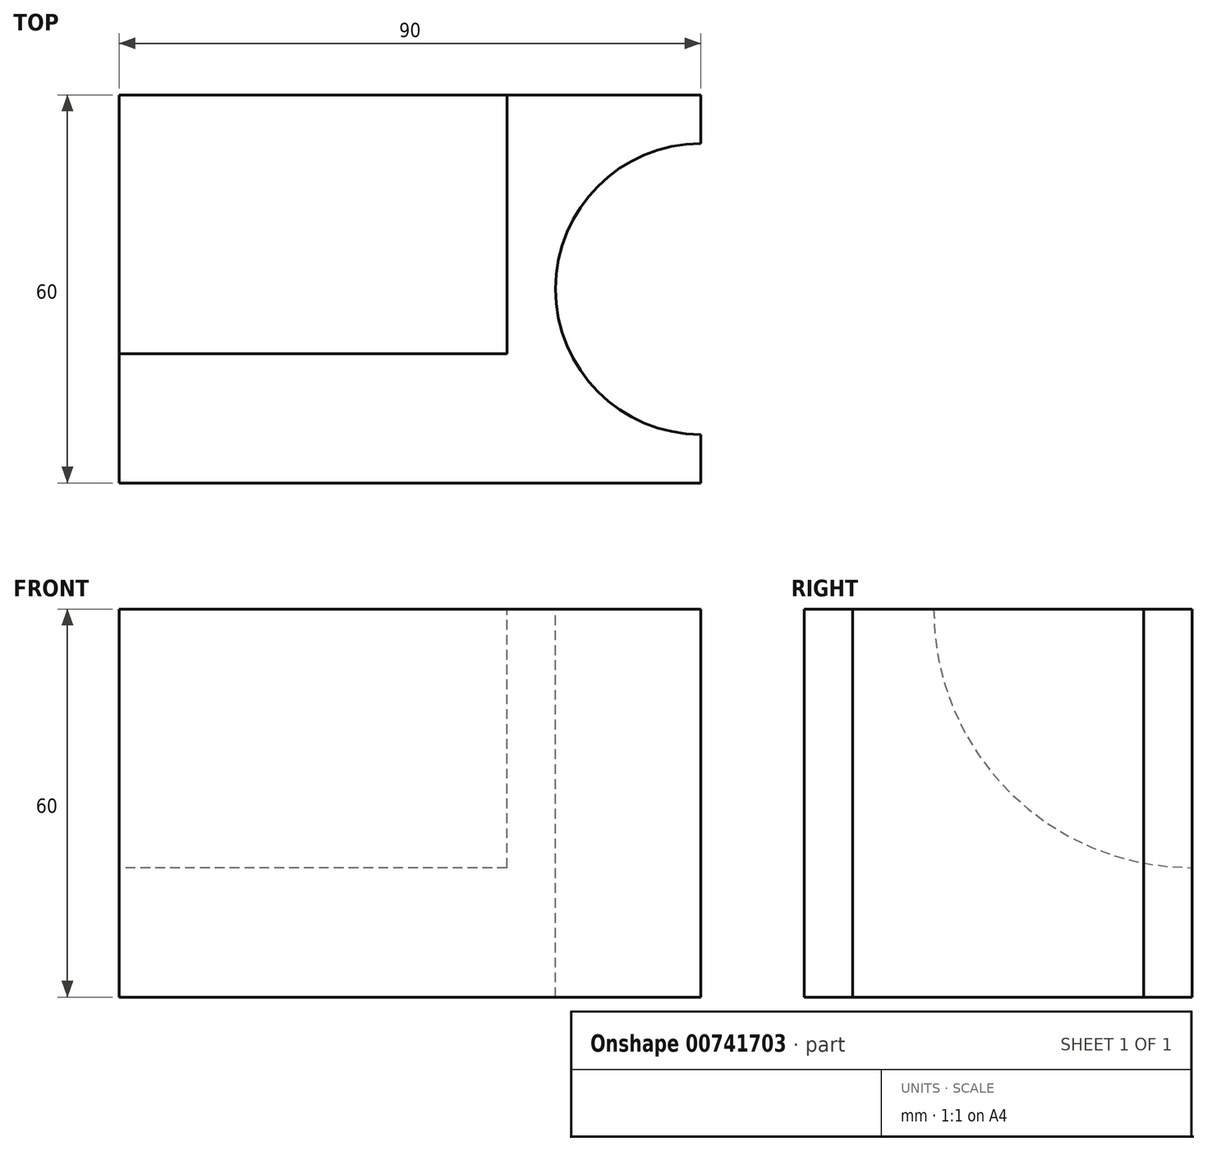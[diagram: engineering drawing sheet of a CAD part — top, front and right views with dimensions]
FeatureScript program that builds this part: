
annotation { "Feature Type Name" : "Feature", "Feature Type Description" : "" }
export const myFeature = defineFeature(function(context is Context, id is Id, definition is map)
    precondition{}
    {
        {
            var Q0;
            Q0=qCreatedBy(makeId("Front.planeOp"),FACE);
            var sketch = newSketch(context, id + "F0", { "sketchPlane" : qUnion([Q0])});
            skLineSegment(sketch, "E0.bottom", {"start": v(-45, -30) * mm, "end": v(45, -30) * mm});
            skLineSegment(sketch, "E0.top", {"start": v(-45, 30) * mm, "end": v(45, 30) * mm});
            skLineSegment(sketch, "E0.left", {"start": v(-45, -30) * mm, "end": v(-45, 30) * mm});
            skLineSegment(sketch, "E0.right", {"start": v(45, -30) * mm, "end": v(45, 30) * mm});
            skPoint(sketch, "E0.middle", {"position": v(0, 0) * mm});
            skSolve(sketch);
        }
        {
            var Q0;
            Q0=makeQuery(id+"F0.imprint","IMPRINT",FACE,{"disambiguationData":[TD([[makeQuery(id+"F0.imprint","IMPRINT",EDGE,{"derivedFrom":sQuery(id+"F0.wireOp",EDGE,"E0.bottom")}),1.0]])]});
            extrude(context, id + "F1", {"entities" : qUnion([Q0]), "depth" : 60 * mm, "offsetDistance" : 25 * mm});
        }
        {
            var Q0;
            Q0=makeQuery(id+"F1.opExtrude","SWEPT_FACE",FACE,{"disambiguationData":[OSD([sQuery(id+"F0.wireOp",EDGE,"E0.top")])]});
            var sketch = newSketch(context, id + "F2", { "sketchPlane" : qUnion([Q0])});
            skArc(sketch, "E1", {"start": v(45, -7.5) * mm, "mid": v(22.5, -30) * mm, "end": v(45, -52.5) * mm});
            skSolve(sketch);
        }
        {
            var Q0;
            {var subQ0=sQuery(id+"F2.wireOp",EDGE,"E1");Q0=makeQuery(id+"F2.imprint","IMPRINT",FACE,{"disambiguationData":[TD([[makeQuery(id+"F2.imprint","IMPRINT",EDGE,{"derivedFrom":subQ0}),1.0]])]});}
            extrude(context, id + "F3", {"entities" : qUnion([Q0]), "operationType" : NewBodyOperationType.REMOVE, "endBound" : BoundingType.THROUGH_ALL, "oppositeDirection" : true, "depth" : 25 * mm, "offsetDistance" : 25 * mm});
        }
        {
            var Q0;
            Q0=makeQuery(id+"F1.opExtrude","SWEPT_FACE",FACE,{"disambiguationData":[OSD([sQuery(id+"F0.wireOp",EDGE,"E0.left")])]});
            var sketch = newSketch(context, id + "F4", { "sketchPlane" : qUnion([Q0])});
            skArc(sketch, "E2", {"start": v(0, -10) * mm, "mid": v(28.28, 1.72) * mm, "end": v(40, 30) * mm});
            skSolve(sketch);
        }
        {
            var Q0;
            {var subQ0=sQuery(id+"F4.wireOp",EDGE,"E2");Q0=makeQuery(id+"F4.imprint","IMPRINT",FACE,{"disambiguationData":[TD([[makeQuery(id+"F4.imprint","IMPRINT",EDGE,{"derivedFrom":subQ0}),1.0]])]});}
            extrude(context, id + "F5", {"entities" : qUnion([Q0]), "operationType" : NewBodyOperationType.REMOVE, "oppositeDirection" : true, "depth" : 60 * mm, "offsetDistance" : 25 * mm});
        }
    });
